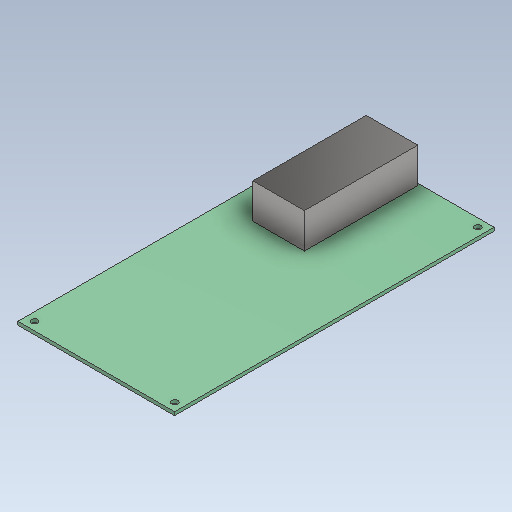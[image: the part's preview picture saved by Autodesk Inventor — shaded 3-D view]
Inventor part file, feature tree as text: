
AUTODESK INVENTOR PART (.ipt)
format: ipt  version: 2021 (Build 250183000, 183)  size: 126,464 bytes
history: native  units: mm
features: extrude x2, sketch x2
ambient origin geometry x8: Origin, YZ Plane, XZ Plane, XY Plane, X Axis, Y Axis, Z Axis, Center Point
bodies: Solid1 (feature_tree)
feature tree (4):
  extrude  "Extrusion1"  Depth=155.0mm
  extrude  "Extrusion2"  Depth=17.0mm
  sketch  "Sketch1"  dims[d0=76.0mm d1=155.0mm]
  sketch  "Sketch2"  dims[d2=68.0mm d3=147.0mm d4=3.1mm d5=3.1mm d6=3.1mm d7=3.1mm d8=1.65mm d9=0.0mm d10=25.0mm d11=55.0mm d12=56.0mm d13=40.0mm d14=17.0mm d15=0.0mm]
